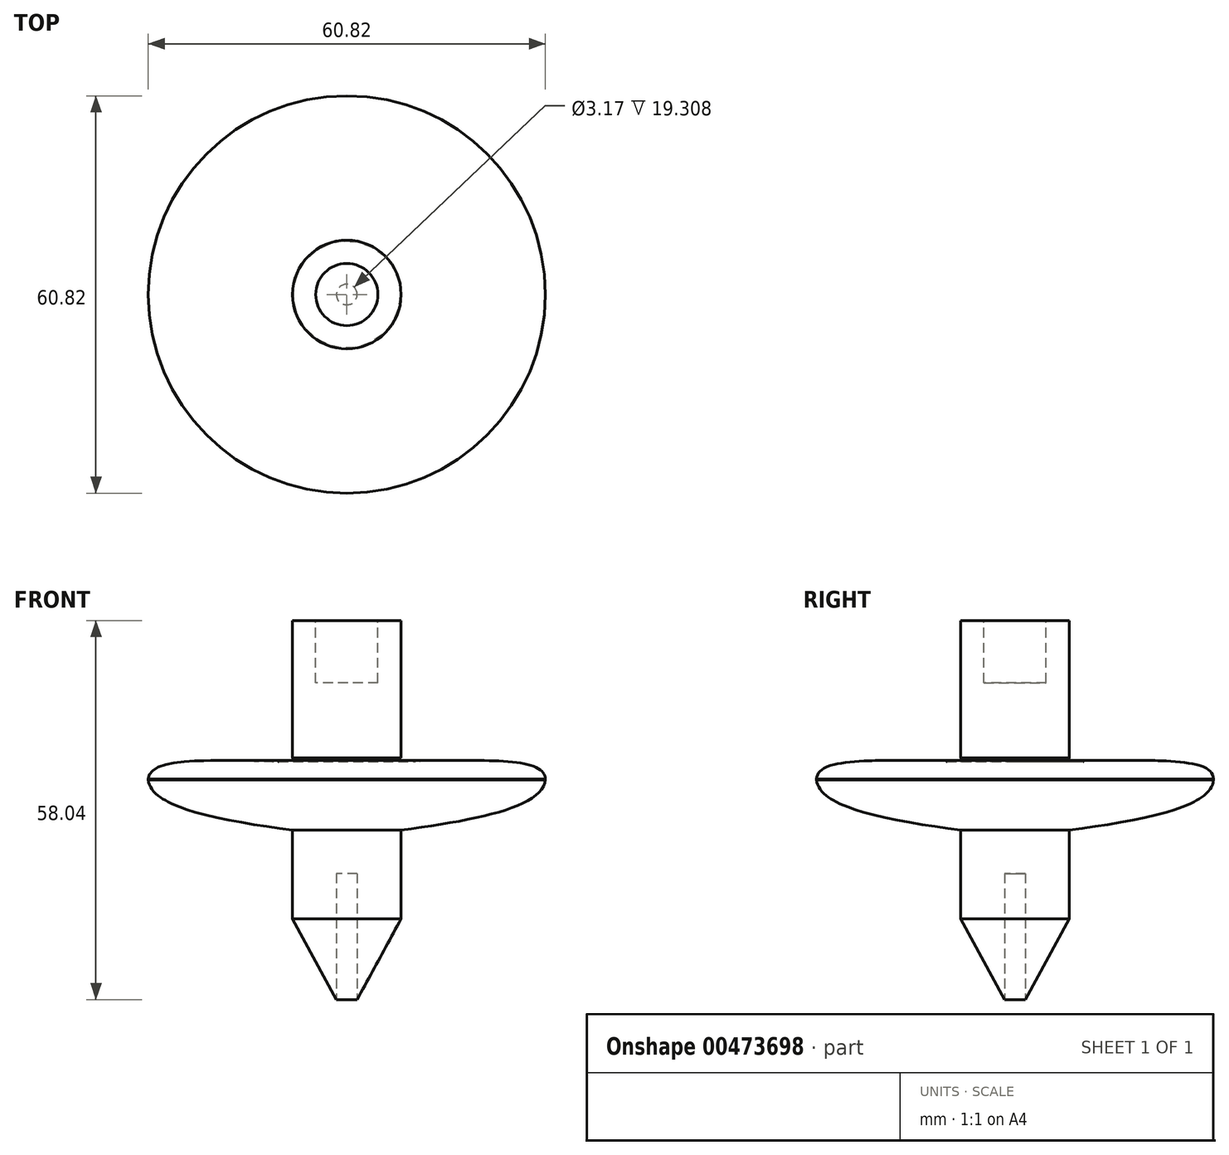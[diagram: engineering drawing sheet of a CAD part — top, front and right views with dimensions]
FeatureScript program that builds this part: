
annotation { "Feature Type Name" : "Feature", "Feature Type Description" : "" }
export const myFeature = defineFeature(function(context is Context, id is Id, definition is map)
    precondition{}
    {
        {
            var Q0;
            Q0=qCreatedBy(makeId("Front.planeOp"),FACE);
            var sketch = newSketch(context, id + "F0", { "sketchPlane" : qUnion([Q0])});
            skLineSegment(sketch, "E0", {"start": v(0, 0) * mm, "end": v(8.32, 15.28) * mm});
            skLineSegment(sketch, "E1", {"start": v(8.32, 15.28) * mm, "end": v(8.32, 28.84) * mm});
            skFitSpline(sketch, "E2", {"points": [v(8.32, 28.84) * mm, v(29.69, 34.9) * mm, v(28.97, 38.48) * mm, v(8.32, 39.55) * mm, v(8.32, 39.9) * mm], "startDerivative": vector(77.71, 10.67) * mm, "endDerivative": vector(5, 8.16) * mm});
            skLineSegment(sketch, "E3", {"start": v(8.32, 39.9) * mm, "end": v(8.32, 60.96) * mm});
            skLineSegment(sketch, "E4", {"start": v(8.32, 60.96) * mm, "end": v(0, 60.96) * mm});
            skLineSegment(sketch, "E5", {"start": v(0, 60.96) * mm, "end": v(0, 0) * mm});
            skLineSegment(sketch, "E6", {"start": v(30.41, 36.58) * mm, "end": v(30.41, 41.44) * mm});
            skLineSegment(sketch, "E7", {"start": v(30.41, 36.58) * mm, "end": v(30.41, 32.5) * mm});
            skSolve(sketch);
        }
        {
            var Q0;
            Q0=makeQuery(id+"F0.imprint","IMPRINT",FACE,{"disambiguationData":[TD([[makeQuery(id+"F0.imprint","IMPRINT",EDGE,{"derivedFrom":sQuery(id+"F0.wireOp",EDGE,"E0")}),1.0]])]});
            var Q1;
            Q1=sQuery(id+"F0.wireOp",EDGE,"E5");
            revolve(context, id + "F1", {"entities" : qUnion([Q0]), "axis" : qUnion([Q1]), "revolveType" : RevolveType.FULL});
        }
        {
            var Q0;
            Q0=makeQuery(id+"F1.opRevolve","SWEPT_FACE",FACE,{"disambiguationData":[OSD([sQuery(id+"F0.wireOp",EDGE,"E4")])]});
            var sketch = newSketch(context, id + "F2", { "sketchPlane" : qUnion([Q0])});
            skCircle(sketch, "E8", {"center": v(0, 0) * mm, "radius": 4.76 * mm});
            skSolve(sketch);
        }
        {
            var Q0;
            Q0=makeQuery(id+"F2.imprint","IMPRINT",FACE,{"disambiguationData":[TD([[makeQuery(id+"F2.imprint","IMPRINT",EDGE,{"derivedFrom":sQuery(id+"F2.wireOp",EDGE,"E8")}),1.0]])]});
            extrude(context, id + "F3", {"entities" : qUnion([Q0]), "operationType" : NewBodyOperationType.REMOVE, "depth" : -9.52 * mm});
        }
        {
            var Q0;
            Q0=makeQuery(id+"F2.imprint","IMPRINT",FACE,{"disambiguationData":[TD([[makeQuery(id+"F2.imprint","IMPRINT",EDGE,{"derivedFrom":sQuery(id+"F2.wireOp",EDGE,"E8")}),1.0]])]});
            extrude(context, id + "F4", {"entities" : qUnion([Q0]), "oppositeDirection" : true, "depth" : 9.52 * mm});
        }
        {
            var Q0;
            Q0=qCreatedBy(makeId("Top.planeOp"),FACE);
            var sketch = newSketch(context, id + "F5", { "sketchPlane" : qUnion([Q0])});
            skCircle(sketch, "E9", {"center": v(0, 0) * mm, "radius": 1.59 * mm});
            skSolve(sketch);
        }
        {
            var Q0;
            Q0 = qSketchRegion(id + "F5", true);
            extrude(context, id + "F6", {"entities" : qUnion([Q0]), "operationType" : NewBodyOperationType.REMOVE, "depth" : 22.22 * mm});
        }
    });
